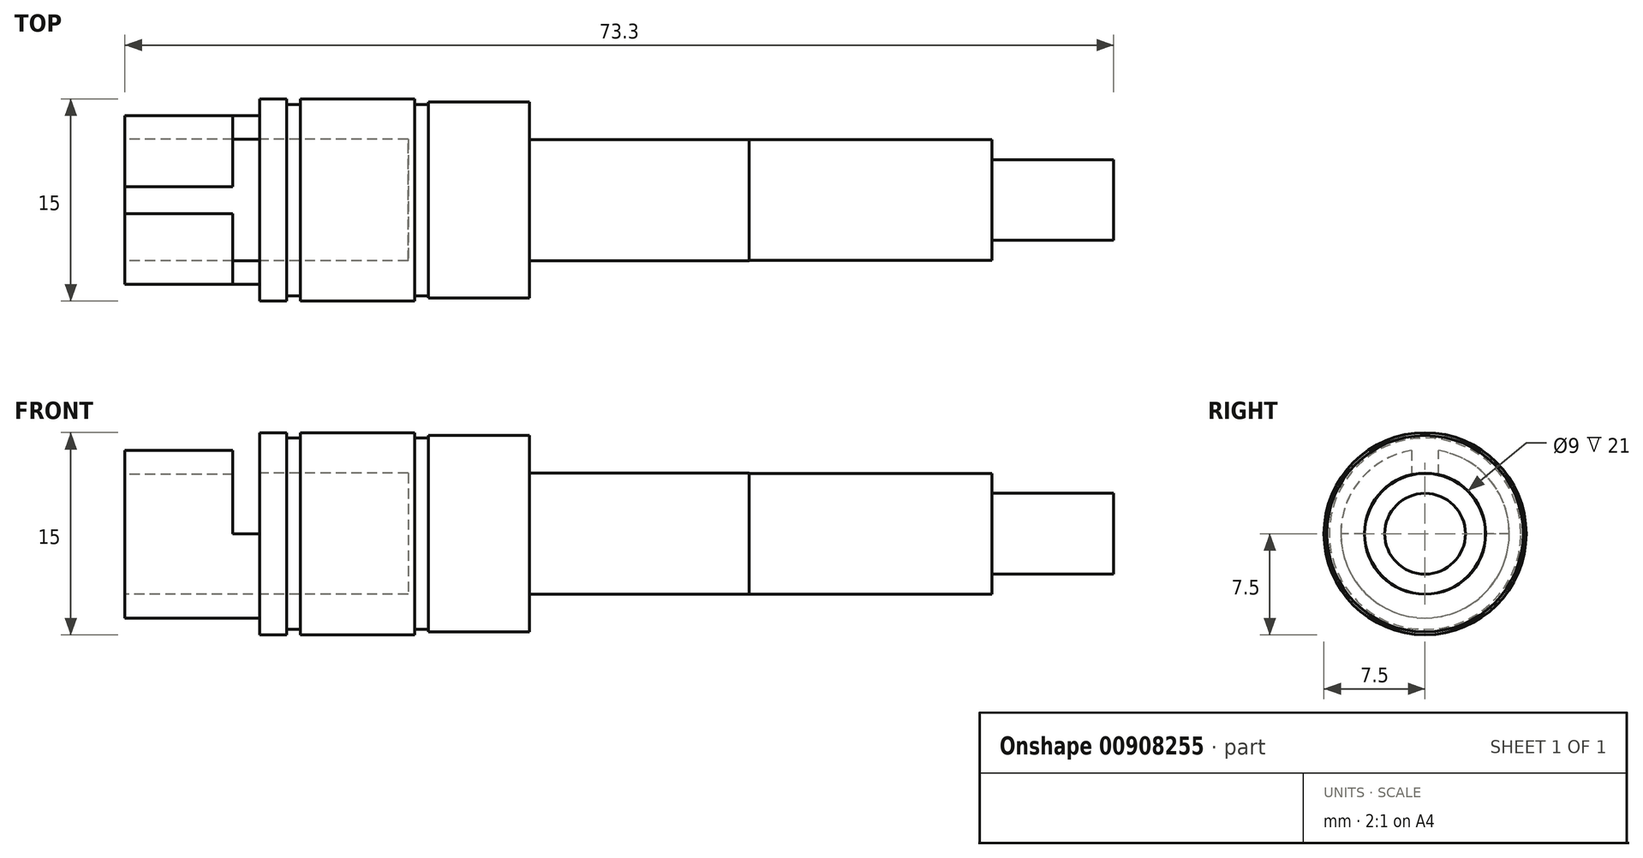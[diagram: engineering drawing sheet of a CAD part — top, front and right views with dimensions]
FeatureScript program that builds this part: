
annotation { "Feature Type Name" : "Feature", "Feature Type Description" : "" }
export const myFeature = defineFeature(function(context is Context, id is Id, definition is map)
    precondition{}
    {
        {
            var Q0;
            Q0=qCreatedBy(makeId("Front.planeOp"),FACE);
            var sketch = newSketch(context, id + "F0", { "sketchPlane" : qUnion([Q0])});
            skLineSegment(sketch, "E0", {"start": v(0, 0) * mm, "end": v(125.81, 0) * mm, "construction": true});
            skLineSegment(sketch, "E1", {"start": v(0, 4.5) * mm, "end": v(0, 6.25) * mm});
            skLineSegment(sketch, "E2", {"start": v(0, 6.25) * mm, "end": v(10, 6.25) * mm});
            skLineSegment(sketch, "E3", {"start": v(10, 6.25) * mm, "end": v(10, 7.5) * mm});
            skLineSegment(sketch, "E4", {"start": v(10, 7.5) * mm, "end": v(12, 7.5) * mm});
            skLineSegment(sketch, "E5", {"start": v(12, 7.5) * mm, "end": v(12, 7.1) * mm});
            skLineSegment(sketch, "E6", {"start": v(12, 7.1) * mm, "end": v(13, 7.1) * mm});
            skLineSegment(sketch, "E7", {"start": v(13, 7.1) * mm, "end": v(13, 7.5) * mm});
            skLineSegment(sketch, "E8", {"start": v(13, 7.5) * mm, "end": v(21.5, 7.5) * mm});
            skLineSegment(sketch, "E9", {"start": v(21.5, 7.5) * mm, "end": v(21.5, 7.1) * mm});
            skLineSegment(sketch, "E10", {"start": v(21.5, 7.1) * mm, "end": v(22.5, 7.1) * mm});
            skLineSegment(sketch, "E11", {"start": v(22.5, 7.1) * mm, "end": v(22.5, 7.28) * mm});
            skLineSegment(sketch, "E12", {"start": v(22.5, 7.28) * mm, "end": v(30, 7.28) * mm});
            skLineSegment(sketch, "E13", {"start": v(30, 7.28) * mm, "end": v(30, 4.5) * mm});
            skLineSegment(sketch, "E14", {"start": v(30, 4.5) * mm, "end": v(46.3, 4.5) * mm});
            skLineSegment(sketch, "E15", {"start": v(46.3, 4.5) * mm, "end": v(46.3, 4.47) * mm});
            skLineSegment(sketch, "E16", {"start": v(46.3, 4.47) * mm, "end": v(64.3, 4.47) * mm});
            skLineSegment(sketch, "E17", {"start": v(64.3, 4.47) * mm, "end": v(64.3, 3) * mm});
            skLineSegment(sketch, "E18", {"start": v(64.3, 3) * mm, "end": v(73.3, 3) * mm});
            skLineSegment(sketch, "E19", {"start": v(73.3, 3) * mm, "end": v(73.3, 0) * mm});
            skLineSegment(sketch, "E20", {"start": v(0, 4.5) * mm, "end": v(21, 4.5) * mm});
            skLineSegment(sketch, "E21", {"start": v(21, 4.5) * mm, "end": v(21, 0) * mm});
            skLineSegment(sketch, "E22", {"start": v(21, 0) * mm, "end": v(73.3, 0) * mm});
            skSolve(sketch);
        }
        {
            var Q0;
            Q0=makeQuery(id+"F0.imprint","IMPRINT",FACE,{"disambiguationData":[TD([[makeQuery(id+"F0.imprint","IMPRINT",EDGE,{"derivedFrom":sQuery(id+"F0.wireOp",EDGE,"E1")}),-1.0]])]});
            var Q1;
            Q1=sQuery(id+"F0.wireOp",EDGE,"E0");
            revolve(context, id + "F1", {"surfaceOperationType" : NewSurfaceOperationType.NEW, "entities" : qUnion([Q0]), "axis" : qUnion([Q1]), "revolveType" : RevolveType.FULL});
        }
        {
            var Q0;
            Q0=qCreatedBy(makeId("Front.planeOp"),FACE);
            var sketch = newSketch(context, id + "F2", { "sketchPlane" : qUnion([Q0])});
            skLineSegment(sketch, "E23.bottom", {"start": v(8, 7.5) * mm, "end": v(10, 7.5) * mm});
            skLineSegment(sketch, "E23.top", {"start": v(8, 0) * mm, "end": v(10, 0) * mm});
            skLineSegment(sketch, "E23.left", {"start": v(8, 7.5) * mm, "end": v(8, 0) * mm});
            skLineSegment(sketch, "E23.right", {"start": v(10, 7.5) * mm, "end": v(10, 0) * mm});
            skSolve(sketch);
        }
        {
            var Q0;
            Q0 = qSketchRegion(id + "F2", true);
            extrude(context, id + "F3", {"entities" : qUnion([Q0]), "operationType" : NewBodyOperationType.REMOVE, "endBound" : BoundingType.THROUGH_ALL, "oppositeDirection" : true, "depth" : 25 * mm, "offsetDistance" : 25 * mm, "hasSecondDirection" : true, "secondDirectionBound" : SecondDirectionBoundingType.THROUGH_ALL, "secondDirectionOppositeDirection" : false, "secondDirectionDepth" : 25 * mm});
        }
        {
            var Q0;
            Q0=makeQuery(id+"F1.opRevolve","SWEPT_FACE",FACE,{"disambiguationData":[OSD([sQuery(id+"F0.wireOp",EDGE,"E1")])]});
            var sketch = newSketch(context, id + "F4", { "sketchPlane" : qUnion([Q0])});
            skLineSegment(sketch, "E24.bottom", {"start": v(-1, 7.5) * mm, "end": v(1, 7.5) * mm});
            skLineSegment(sketch, "E24.top", {"start": v(-1, 0) * mm, "end": v(1, 0) * mm});
            skLineSegment(sketch, "E24.left", {"start": v(-1, 7.5) * mm, "end": v(-1, 0) * mm});
            skLineSegment(sketch, "E24.right", {"start": v(1, 7.5) * mm, "end": v(1, 0) * mm});
            skSolve(sketch);
        }
        {
            var Q0;
            Q0 = qSketchRegion(id + "F4", true);
            var Q1;
            Q1=makeQuery(id+"F3.boolean.opBoolean","COPY",FACE,{"derivedFrom":makeQuery(id+"F3.opExtrude","SWEPT_FACE",FACE,{"disambiguationData":[OSD([sQuery(id+"F2.wireOp",EDGE,"E23.left")])]})});
            extrude(context, id + "F5", {"entities" : qUnion([Q0]), "operationType" : NewBodyOperationType.REMOVE, "endBound" : BoundingType.UP_TO_SURFACE, "oppositeDirection" : true, "depth" : 25 * mm, "endBoundEntityFace" : qUnion([Q1]), "offsetDistance" : 25 * mm});
        }
    });
